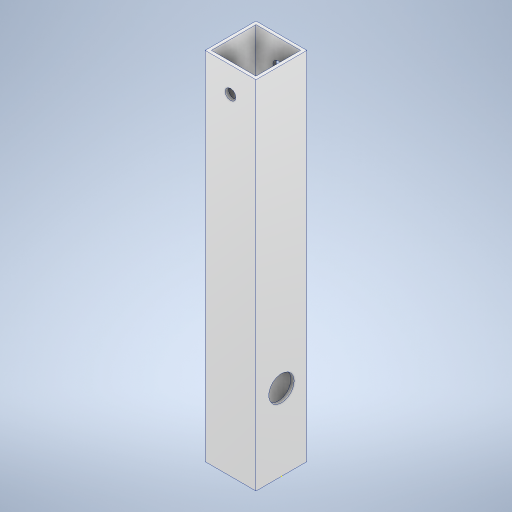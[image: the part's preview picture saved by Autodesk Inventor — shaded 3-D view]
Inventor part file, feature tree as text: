
AUTODESK INVENTOR PART (.ipt)
format: ipt  version: 2024 (Build 280153000, 153)  size: 282,624 bytes
history: native  units: mm
features: extrude x5, sketch x5
ambient origin geometry x8: Origin, YZ Plane, XZ Plane, XY Plane, X Axis, Y Axis, Z Axis, Center Point
bodies: Solid1 (feature_tree)
feature tree (10):
  extrude  "Extrusion1"  Depth=25.4mm
  extrude  "Extrusion2"  Depth=1.5875mm
  extrude  "Extrusion3"  Depth=38.1mm
  sketch  "Sketch4"  dims[d4=660.4mm d5=0.0mm d6=38.1mm]
  extrude  "Extrusion4"  Depth=8.73125mm
  extrude  "Extrusion5"  Depth=177.8mm
  sketch  "Sketch2"  dims[d0=25.4mm d1=25.4mm]
  sketch  "Sketch3"  dims[d2=1.5875mm d3=1.5875mm]
  sketch  "Sketch5"  dims[d7=9.525mm d8=8.73125mm]
  sketch  "Sketch6"  dims[d9=46.600008mm d10=0.0mm d11=177.8mm d12=354.849999mm d13=0.0mm d14=12.7mm d15=5.2578mm d16=86.100006mm d17=0.0mm d18=12.7mm d19=44.35mm d20=0.0mm]
